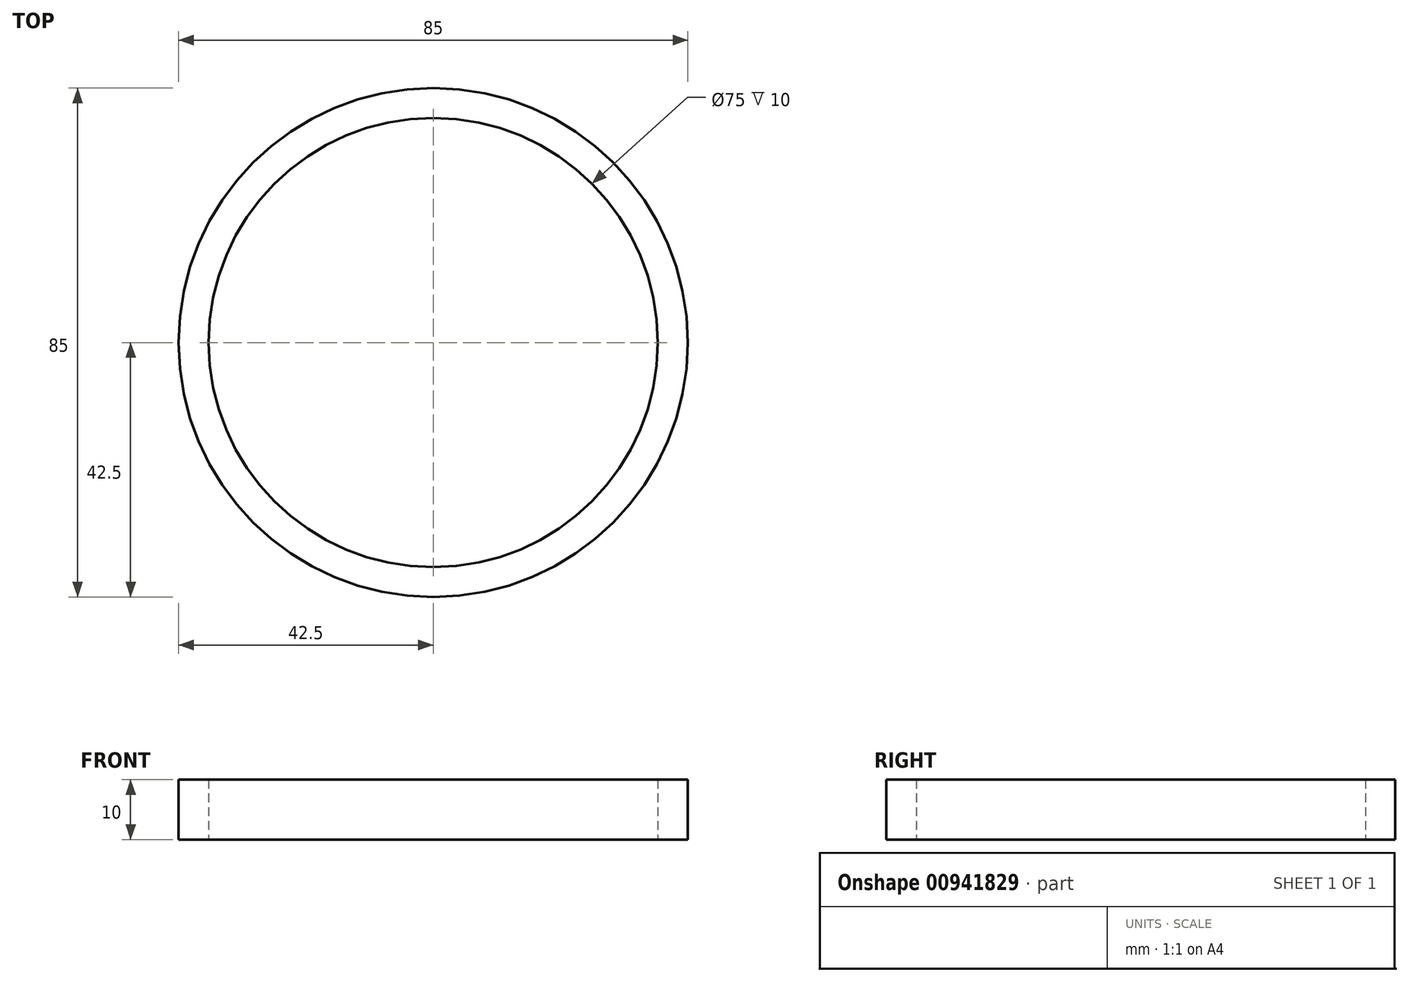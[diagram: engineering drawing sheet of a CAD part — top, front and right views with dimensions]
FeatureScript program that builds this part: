
annotation { "Feature Type Name" : "Feature", "Feature Type Description" : "" }
export const myFeature = defineFeature(function(context is Context, id is Id, definition is map)
    precondition{}
    {
        {
            var Q0;
            Q0=qCreatedBy(makeId("Top.planeOp"),FACE);
            var sketch = newSketch(context, id + "F0", { "sketchPlane" : qUnion([Q0])});
            skCircle(sketch, "E0", {"center": v(0, 0) * mm, "radius": 37.5 * mm});
            skCircle(sketch, "E1", {"center": v(0, 0) * mm, "radius": 42.5 * mm});
            skSolve(sketch);
        }
        {
            var Q0;
            Q0=makeQuery(id+"F0.imprint","IMPRINT",FACE,{"disambiguationData":[TD([[makeQuery(id+"F0.imprint","IMPRINT",EDGE,{"derivedFrom":sQuery(id+"F0.wireOp",EDGE,"E0")}),-1.0]])]});
            extrude(context, id + "F1", {"entities" : qUnion([Q0]), "depth" : 10 * mm, "offsetDistance" : 25 * mm});
        }
    });
